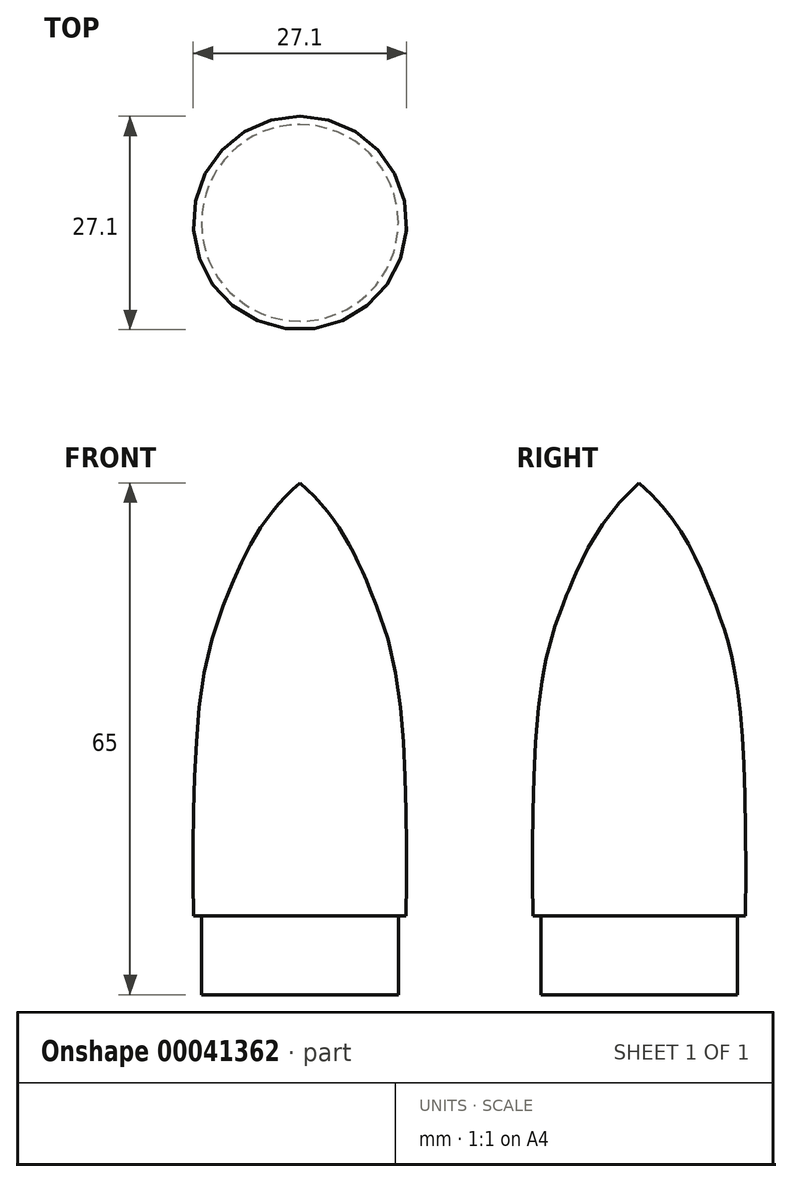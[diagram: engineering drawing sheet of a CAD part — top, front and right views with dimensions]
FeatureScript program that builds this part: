
annotation { "Feature Type Name" : "Feature", "Feature Type Description" : "" }
export const myFeature = defineFeature(function(context is Context, id is Id, definition is map)
    precondition{}
    {
        {
            var Q0;
            Q0=qCreatedBy(makeId("Right.planeOp"),FACE);
            var sketch = newSketch(context, id + "F0", { "sketchPlane" : qUnion([Q0])});
            skLineSegment(sketch, "E0", {"start": v(0, 0) * mm, "end": v(12.5, 0) * mm});
            skLineSegment(sketch, "E1", {"start": v(12.5, 0) * mm, "end": v(12.5, 10) * mm});
            skLineSegment(sketch, "E2", {"start": v(12.5, 10) * mm, "end": v(13.5, 10) * mm});
            skLineSegment(sketch, "E3", {"start": v(0, 0) * mm, "end": v(0, 65) * mm});
            skFitSpline(sketch, "E4", {"points": [v(0, 65) * mm, v(9.1, 51.03) * mm, v(13.5, 10) * mm], "startDerivative": vector(38.9, -33.4) * mm, "endDerivative": vector(-1.93, -139.47) * mm});
            skSolve(sketch);
        }
        {
            var Q0;
            Q0=makeQuery(id+"F0.imprint","IMPRINT",FACE,{"disambiguationData":[TD([[makeQuery(id+"F0.imprint","IMPRINT",EDGE,{"derivedFrom":sQuery(id+"F0.wireOp",EDGE,"E0")}),1.0]])]});
            var Q1;
            Q1=sQuery(id+"F0.wireOp",EDGE,"E3");
            revolve(context, id + "F1", {"entities" : qUnion([Q0]), "axis" : qUnion([Q1]), "revolveType" : RevolveType.FULL});
        }
    });
